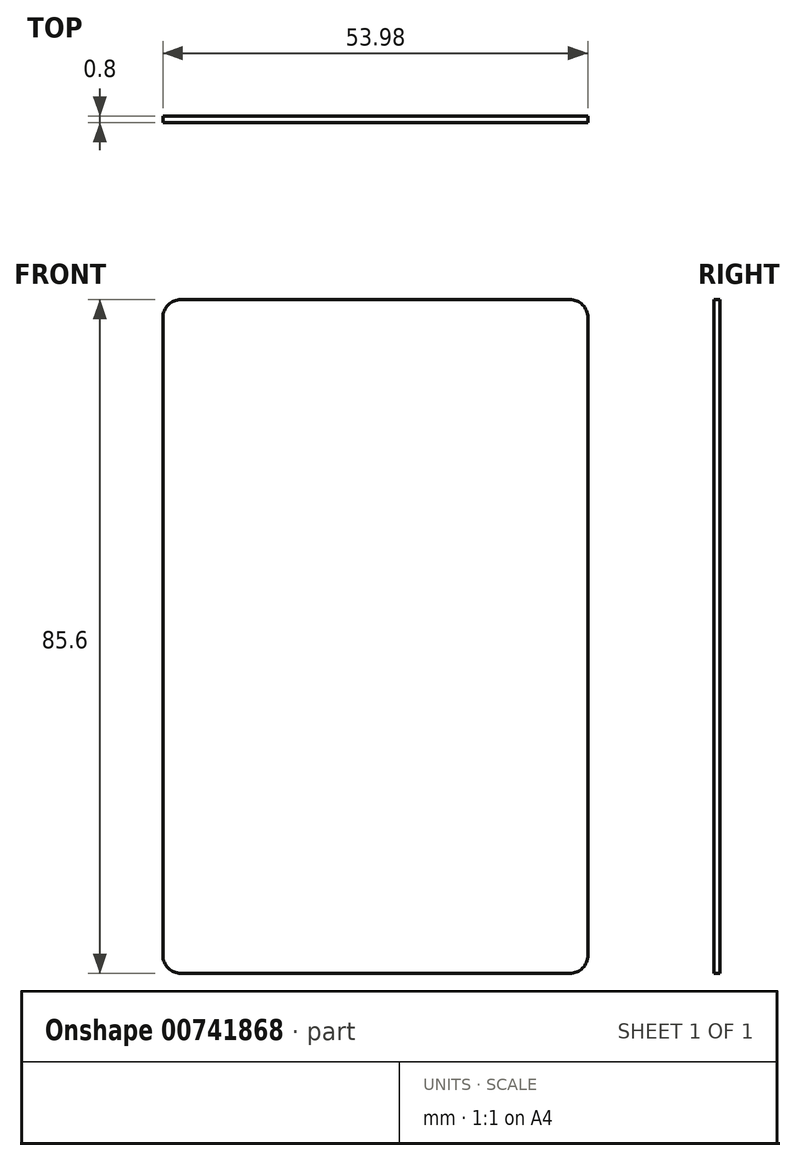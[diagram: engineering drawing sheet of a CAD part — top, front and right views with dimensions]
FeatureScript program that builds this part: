
annotation { "Feature Type Name" : "Feature", "Feature Type Description" : "" }
export const myFeature = defineFeature(function(context is Context, id is Id, definition is map)
    precondition{}
    {
        {
            var Q0;
            Q0=qCreatedBy(makeId("Front.planeOp"),FACE);
            var sketch = newSketch(context, id + "F0", { "sketchPlane" : qUnion([Q0])});
            skLineSegment(sketch, "E0.bottom", {"start": v(-53.98, 85.6) * mm, "end": v(0, 85.6) * mm});
            skLineSegment(sketch, "E0.top", {"start": v(-53.98, 0) * mm, "end": v(0, 0) * mm});
            skLineSegment(sketch, "E0.left", {"start": v(-53.98, 85.6) * mm, "end": v(-53.98, 0) * mm});
            skLineSegment(sketch, "E0.right", {"start": v(0, 85.6) * mm, "end": v(0, 0) * mm});
            skSolve(sketch);
        }
        {
            var Q0;
            Q0 = qSketchRegion(id + "F0", true);
            extrude(context, id + "F1", {"entities" : qUnion([Q0]), "depth" : 0.8 * mm, "offsetDistance" : 25.4 * mm});
        }
        {
            var Q0;
            Q0=makeQuery(id+"F1.opExtrude","SWEPT_EDGE",EDGE,{"disambiguationData":[OSD([sQuery(id+"F0.wireOp",EDGE,"E0.bottom"),sQuery(id+"F0.wireOp",EDGE,"E0.right")])]});
            var Q1;
            Q1=makeQuery(id+"F1.opExtrude","SWEPT_EDGE",EDGE,{"disambiguationData":[OSD([sQuery(id+"F0.wireOp",EDGE,"E0.top"),sQuery(id+"F0.wireOp",EDGE,"E0.right")])]});
            var Q2;
            Q2=makeQuery(id+"F1.opExtrude","SWEPT_EDGE",EDGE,{"disambiguationData":[OSD([sQuery(id+"F0.wireOp",EDGE,"E0.top"),sQuery(id+"F0.wireOp",EDGE,"E0.left")])]});
            var Q3;
            Q3=makeQuery(id+"F1.opExtrude","SWEPT_EDGE",EDGE,{"disambiguationData":[OSD([sQuery(id+"F0.wireOp",EDGE,"E0.bottom"),sQuery(id+"F0.wireOp",EDGE,"E0.left")])]});
            fillet(context, id + "F2", {"entities" : qUnion([Q0, Q1, Q2, Q3]), "radius" : 2.3 * mm, "tangentPropagation" : true, "allowEdgeOverflow" : false});
        }
    });
